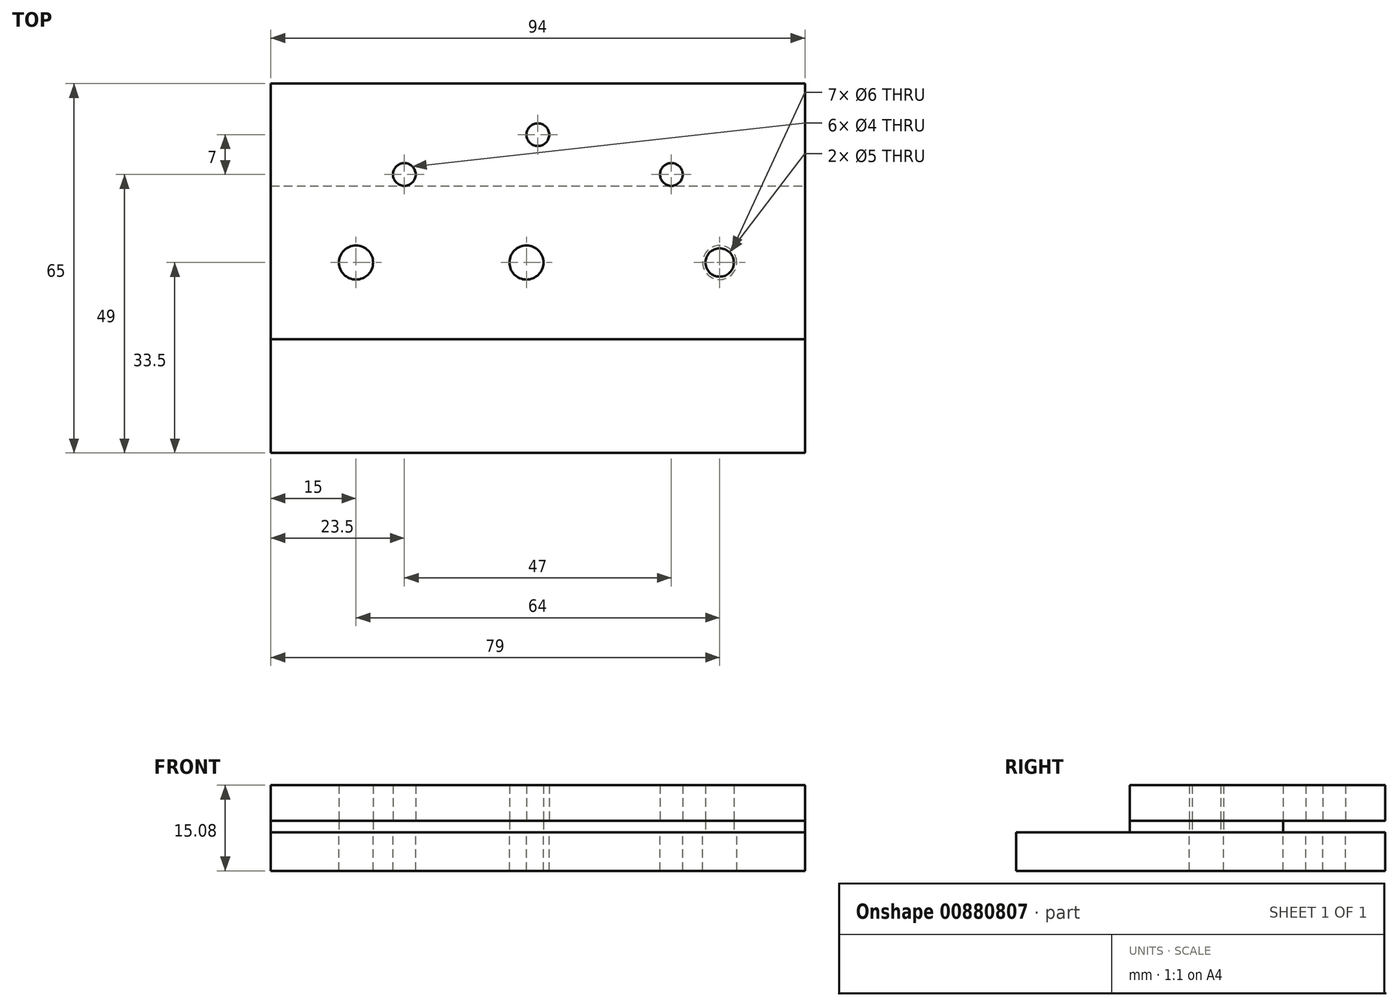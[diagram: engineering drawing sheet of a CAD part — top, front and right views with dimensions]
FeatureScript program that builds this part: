
annotation { "Feature Type Name" : "Feature", "Feature Type Description" : "" }
export const myFeature = defineFeature(function(context is Context, id is Id, definition is map)
    precondition{}
    {
        {
            var Q0;
            Q0=qCreatedBy(makeId("Top.planeOp"),FACE);
            var sketch = newSketch(context, id + "F0", { "sketchPlane" : qUnion([Q0])});
            skLineSegment(sketch, "E0.bottom", {"start": v(-141.5, 13.5) * mm, "end": v(-77.5, 13.5) * mm});
            skLineSegment(sketch, "E0.top", {"start": v(-141.5, -13.5) * mm, "end": v(-77.5, -13.5) * mm});
            skLineSegment(sketch, "E1", {"start": v(-77.5, 13.5) * mm, "end": v(-77.5, -13.5) * mm});
            skLineSegment(sketch, "E2", {"start": v(77.5, 13.5) * mm, "end": v(77.5, -13.5) * mm, "construction": true});
            skLineSegment(sketch, "E3", {"start": v(-141.5, 0) * mm, "end": v(-111.5, 0) * mm, "construction": true});
            skCircle(sketch, "E4", {"center": v(-126.5, 0) * mm, "radius": 3 * mm});
            skCircle(sketch, "E5", {"center": v(-92.5, 0) * mm, "radius": 10 * mm, "construction": true});
            skCircle(sketch, "E6", {"center": v(-92.5, 0) * mm, "radius": 2.5 * mm});
            skLineSegment(sketch, "E7", {"start": v(-141.5, 13.5) * mm, "end": v(-171.5, 13.5) * mm});
            skLineSegment(sketch, "E8", {"start": v(-171.5, 13.5) * mm, "end": v(-171.5, -13.5) * mm});
            skLineSegment(sketch, "E9", {"start": v(-171.5, -13.5) * mm, "end": v(-141.5, -13.5) * mm});
            skCircle(sketch, "E10.MirrorC", {"center": v(-156.5, 0) * mm, "radius": 3 * mm});
            skSolve(sketch);
        }
        {
            var Q0;
            Q0 = qSketchRegion(id + "F0", true);
            extrude(context, id + "F1", {"entities" : qUnion([Q0]), "depth" : 2 * mm, "offsetDistance" : 25 * mm});
        }
        {
            var Q0;
            Q0=makeQuery(id+"F1.opExtrude","CAP_FACE",FACE,{"disambiguationData":[OSD([sQuery(id+"F0.wireOp",EDGE,"E0.bottom"),sQuery(id+"F0.wireOp",EDGE,"E0.top"),sQuery(id+"F0.wireOp",EDGE,"E0.right"),sQuery(id+"F0.wireOp",EDGE,"E4"),sQuery(id+"F0.wireOp",EDGE,"E6"),sQuery(id+"F0.wireOp",EDGE,"E7"),sQuery(id+"F0.wireOp",EDGE,"E8"),sQuery(id+"F0.wireOp",EDGE,"E9"),sQuery(id+"F0.wireOp",EDGE,"E10.MirrorC")])],"isStart":true});
            var sketch = newSketch(context, id + "F2", { "sketchPlane" : qUnion([Q0])});
            skLineSegment(sketch, "E11.0", {"start": v(-171.5, -13.5) * mm, "end": v(-171.5, 13.5) * mm});
            skLineSegment(sketch, "E12", {"start": v(-171.5, -13.5) * mm, "end": v(-171.5, -31.5) * mm});
            skLineSegment(sketch, "E13.0", {"start": v(-77.5, -13.5) * mm, "end": v(-77.5, 13.5) * mm});
            skLineSegment(sketch, "E14", {"start": v(-77.5, -13.5) * mm, "end": v(-77.5, -31.5) * mm});
            skLineSegment(sketch, "E15", {"start": v(-171.5, 13.5) * mm, "end": v(-171.5, 33.5) * mm});
            skLineSegment(sketch, "E16", {"start": v(-171.5, 33.5) * mm, "end": v(-77.5, 33.5) * mm});
            skLineSegment(sketch, "E17", {"start": v(-77.5, 33.5) * mm, "end": v(-77.5, 13.5) * mm});
            skCircle(sketch, "E18.0", {"center": v(-156.5, 0) * mm, "radius": 3 * mm, "construction": true});
            skCircle(sketch, "E19.0", {"center": v(-126.5, 0) * mm, "radius": 3 * mm, "construction": true});
            skCircle(sketch, "E20.0", {"center": v(-92.5, 0) * mm, "radius": 2.5 * mm, "construction": true});
            skCircle(sketch, "E21", {"center": v(-156.5, 0) * mm, "radius": 3 * mm});
            skCircle(sketch, "E22", {"center": v(-126.5, 0) * mm, "radius": 3 * mm});
            skCircle(sketch, "E23", {"center": v(-92.5, 0) * mm, "radius": 3 * mm});
            skLineSegment(sketch, "E24", {"start": v(-171.5, -31.5) * mm, "end": v(-77.5, -31.5) * mm});
            skLineSegment(sketch, "E25", {"start": v(-124.5, -40.5) * mm, "end": v(-124.5, -13.5) * mm, "construction": true});
            skLineSegment(sketch, "E26", {"start": v(-101, -22.5) * mm, "end": v(-101, -31.5) * mm, "construction": true});
            skLineSegment(sketch, "E27", {"start": v(-148, -22.5) * mm, "end": v(-148, -31.5) * mm, "construction": true});
            skLineSegment(sketch, "E28", {"start": v(-148, -22.5) * mm, "end": v(-148, -11.53) * mm, "construction": true});
            skLineSegment(sketch, "E29", {"start": v(-101, -22.5) * mm, "end": v(-101, -11.07) * mm, "construction": true});
            skLineSegment(sketch, "E30.0", {"start": v(-171.5, -13.5) * mm, "end": v(-77.5, -13.5) * mm, "construction": true});
            skCircle(sketch, "E31", {"center": v(-148, -15.5) * mm, "radius": 2 * mm});
            skCircle(sketch, "E32", {"center": v(-101, -15.5) * mm, "radius": 2 * mm});
            skCircle(sketch, "E33", {"center": v(-124.5, -22.5) * mm, "radius": 2 * mm});
            skPoint(sketch, "E34.orphan", {"position": v(-171.5, -40.5) * mm});
            skPoint(sketch, "E35.end.orphan", {"position": v(-77.5, -40.5) * mm});
            skSolve(sketch);
        }
        {
            var Q0;
            Q0 = qSketchRegion(id + "F2", true);
            extrude(context, id + "F3", {"entities" : qUnion([Q0]), "depth" : 6.78 * mm, "offsetDistance" : 25 * mm});
        }
        {
            var Q0;
            Q0=makeQuery(id+"F1.opExtrude","CAP_FACE",FACE,{"disambiguationData":[OSD([sQuery(id+"F0.wireOp",EDGE,"E0.bottom"),sQuery(id+"F0.wireOp",EDGE,"E0.top"),sQuery(id+"F0.wireOp",EDGE,"E1"),sQuery(id+"F0.wireOp",EDGE,"E4"),sQuery(id+"F0.wireOp",EDGE,"E6"),sQuery(id+"F0.wireOp",EDGE,"E7"),sQuery(id+"F0.wireOp",EDGE,"E8"),sQuery(id+"F0.wireOp",EDGE,"E9"),sQuery(id+"F0.wireOp",EDGE,"E10.MirrorC")])],"isStart":false});
            var sketch = newSketch(context, id + "F4", { "sketchPlane" : qUnion([Q0])});
            skLineSegment(sketch, "E36.0", {"start": v(-171.5, 31.5) * mm, "end": v(-171.5, -13.5) * mm});
            skLineSegment(sketch, "E37.0", {"start": v(-171.5, 31.5) * mm, "end": v(-77.5, 31.5) * mm});
            skLineSegment(sketch, "E38.0", {"start": v(-77.5, -13.5) * mm, "end": v(-77.5, 31.5) * mm});
            skCircle(sketch, "E39.0", {"center": v(-124.5, 22.5) * mm, "radius": 2 * mm});
            skCircle(sketch, "E40.0", {"center": v(-148, 15.5) * mm, "radius": 2 * mm});
            skCircle(sketch, "E41.0", {"center": v(-101, 15.5) * mm, "radius": 2 * mm});
            skCircle(sketch, "E42.0", {"center": v(-156.5, 0) * mm, "radius": 3 * mm});
            skCircle(sketch, "E43.0", {"center": v(-126.5, 0) * mm, "radius": 3 * mm});
            skCircle(sketch, "E44.0", {"center": v(-92.5, 0) * mm, "radius": 2.5 * mm});
            skLineSegment(sketch, "E45.0", {"start": v(-171.5, -13.5) * mm, "end": v(-77.5, -13.5) * mm});
            skPoint(sketch, "E46.orphan", {"position": v(-171.5, -33.5) * mm});
            skPoint(sketch, "E47.orphan", {"position": v(-77.5, -33.5) * mm});
            skSolve(sketch);
        }
        {
            var Q0;
            Q0 = qSketchRegion(id + "F4", true);
            extrude(context, id + "F5", {"entities" : qUnion([Q0]), "depth" : 6.3 * mm, "offsetDistance" : 25 * mm});
        }
    });
